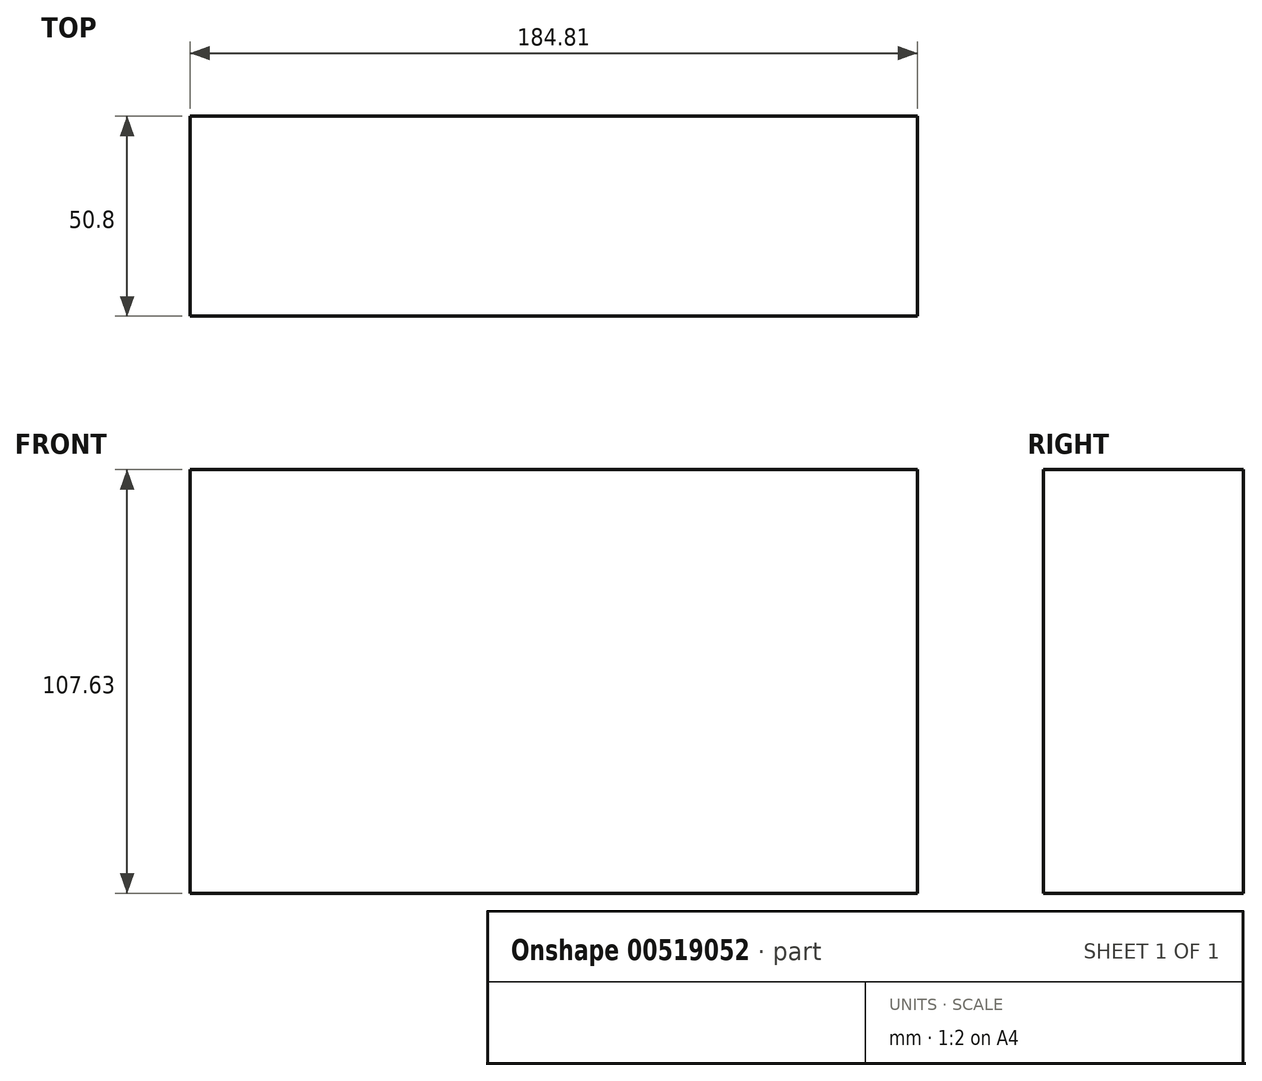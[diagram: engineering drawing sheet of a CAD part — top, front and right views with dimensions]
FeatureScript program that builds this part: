
annotation { "Feature Type Name" : "Feature", "Feature Type Description" : "" }
export const myFeature = defineFeature(function(context is Context, id is Id, definition is map)
    precondition{}
    {
        {
            var Q0;
            Q0=qCreatedBy(makeId("Front.planeOp"),FACE);
            var sketch = newSketch(context, id + "F0", { "sketchPlane" : qUnion([Q0])});
            skLineSegment(sketch, "E0.bottom", {"start": v(-96.66, 52.93) * mm, "end": v(88.15, 52.93) * mm});
            skLineSegment(sketch, "E0.top", {"start": v(-96.66, -54.7) * mm, "end": v(88.15, -54.7) * mm});
            skLineSegment(sketch, "E0.left", {"start": v(-96.66, 52.93) * mm, "end": v(-96.66, -54.7) * mm});
            skLineSegment(sketch, "E0.right", {"start": v(88.15, 52.93) * mm, "end": v(88.15, -54.7) * mm});
            skSolve(sketch);
        }
        {
            var Q0;
            Q0=makeQuery(id+"F0.imprint","IMPRINT",FACE,{"disambiguationData":[TD([[makeQuery(id+"F0.imprint","IMPRINT",EDGE,{"derivedFrom":sQuery(id+"F0.wireOp",EDGE,"E0.bottom")}),-1.0]])]});
            extrude(context, id + "F1", {"entities" : qUnion([Q0]), "depth" : 50.8 * mm, "offsetDistance" : 25.4 * mm});
        }
    });
